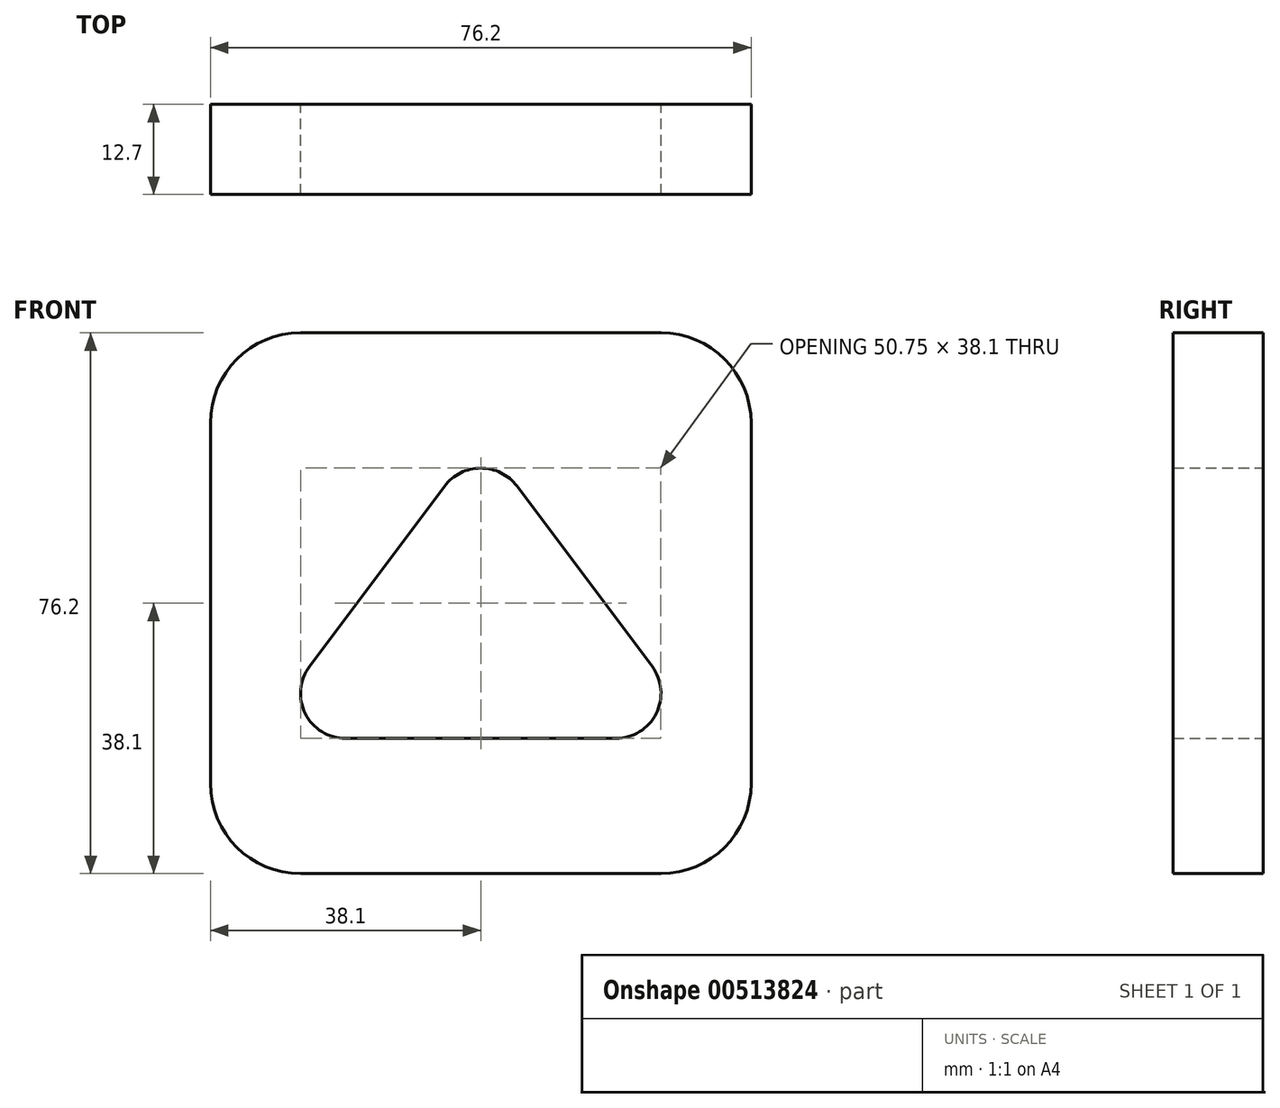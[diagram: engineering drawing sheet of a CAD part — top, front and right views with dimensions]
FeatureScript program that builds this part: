
annotation { "Feature Type Name" : "Feature", "Feature Type Description" : "" }
export const myFeature = defineFeature(function(context is Context, id is Id, definition is map)
    precondition{}
    {
        {
            var Q0;
            Q0=qCreatedBy(makeId("Front.planeOp"),FACE);
            var sketch = newSketch(context, id + "F0", { "sketchPlane" : qUnion([Q0])});
            skLineSegment(sketch, "E0", {"start": v(12.7, 0) * mm, "end": v(63.5, 0) * mm});
            skLineSegment(sketch, "E1", {"start": v(76.2, 12.7) * mm, "end": v(76.2, 63.5) * mm});
            skLineSegment(sketch, "E2", {"start": v(63.5, 76.2) * mm, "end": v(12.7, 76.2) * mm});
            skArc(sketch, "E3", {"start": v(13.97, 29.21) * mm, "mid": v(13.37, 22.56) * mm, "end": v(19.05, 19.05) * mm});
            skArc(sketch, "E4", {"start": v(57.15, 19.05) * mm, "mid": v(62.83, 22.56) * mm, "end": v(62.23, 29.21) * mm});
            skArc(sketch, "E5", {"start": v(43.18, 54.6) * mm, "mid": v(38.1, 57.15) * mm, "end": v(33.02, 54.6) * mm});
            skArc(sketch, "E6", {"start": v(12.7, 76.2) * mm, "mid": v(3.72, 72.48) * mm, "end": v(0, 63.5) * mm});
            skLineSegment(sketch, "E7", {"start": v(0, 63.5) * mm, "end": v(0, 12.7) * mm});
            skArc(sketch, "E8", {"start": v(76.2, 63.5) * mm, "mid": v(72.48, 72.48) * mm, "end": v(63.5, 76.2) * mm});
            skLineSegment(sketch, "E9", {"start": v(33.02, 54.6) * mm, "end": v(13.97, 29.21) * mm});
            skLineSegment(sketch, "E10", {"start": v(57.15, 19.05) * mm, "end": v(19.05, 19.05) * mm});
            skLineSegment(sketch, "E11", {"start": v(62.23, 29.2) * mm, "end": v(43.18, 54.6) * mm});
            skPoint(sketch, "E12.visualSharp", {"position": v(0, 0) * mm});
            skArc(sketch, "E12.filletArc", {"start": v(0, 12.7) * mm, "mid": v(3.72, 3.72) * mm, "end": v(12.7, 0) * mm});
            skPoint(sketch, "E13.visualSharp", {"position": v(76.2, 0) * mm});
            skArc(sketch, "E13.filletArc", {"start": v(63.5, 0) * mm, "mid": v(72.48, 3.72) * mm, "end": v(76.2, 12.7) * mm});
            skSolve(sketch);
        }
        {
            var Q0;
            Q0=makeQuery(id+"F0.imprint","IMPRINT",FACE,{"disambiguationData":[TD([[makeQuery(id+"F0.imprint","IMPRINT",EDGE,{"derivedFrom":sQuery(id+"F0.wireOp",EDGE,"E0")}),1.0]])]});
            extrude(context, id + "F1", {"entities" : qUnion([Q0]), "depth" : 12.7 * mm});
        }
    });
